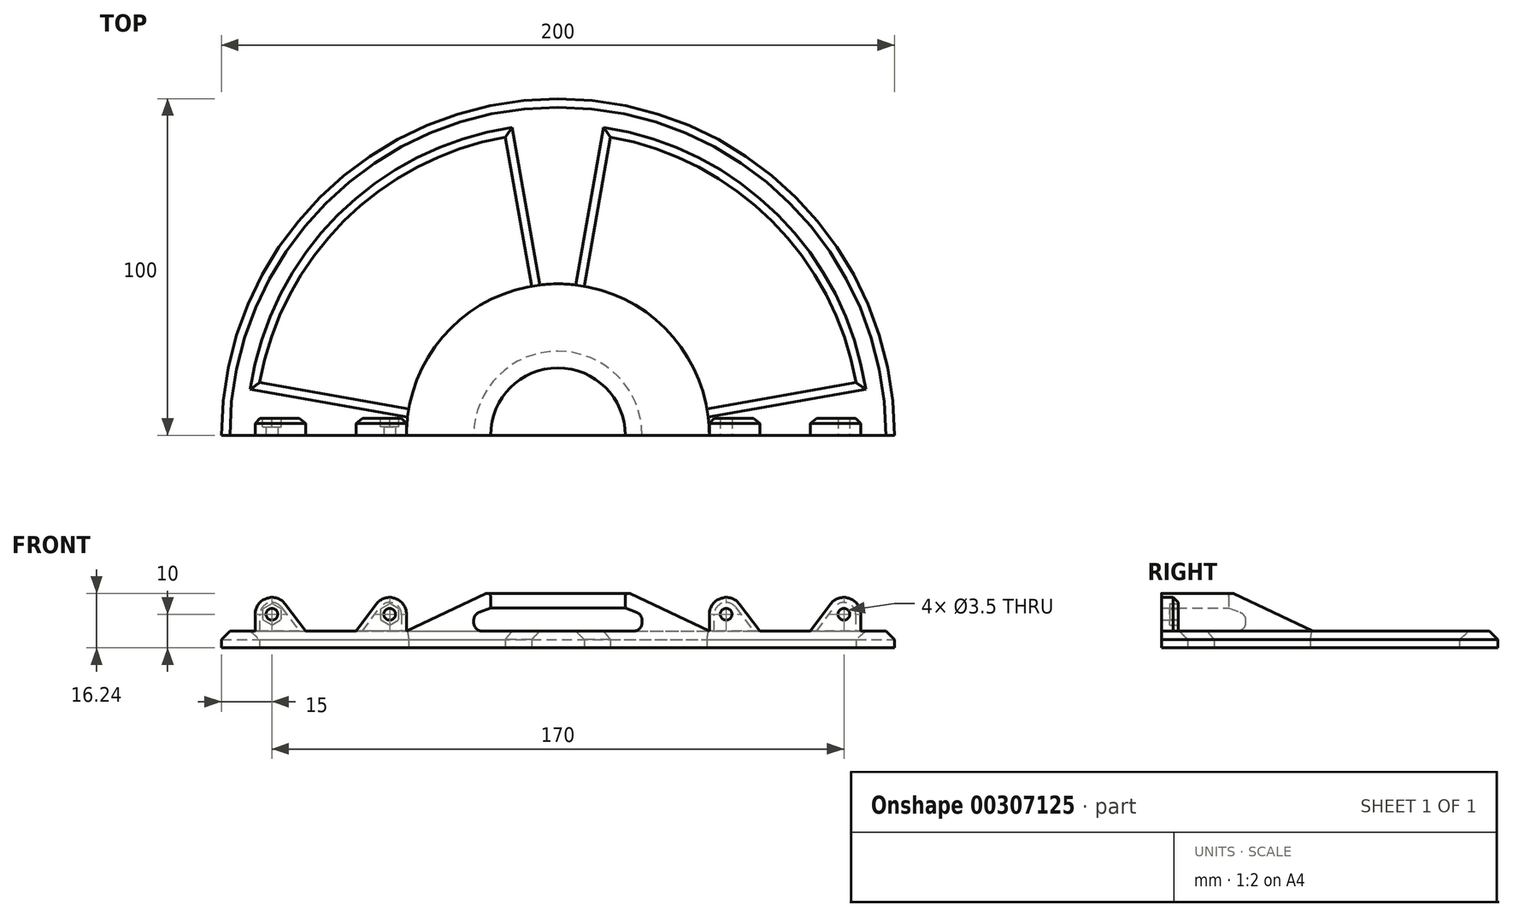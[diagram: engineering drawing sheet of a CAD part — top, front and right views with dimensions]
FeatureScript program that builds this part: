
annotation { "Feature Type Name" : "Feature", "Feature Type Description" : "" }
export const myFeature = defineFeature(function(context is Context, id is Id, definition is map)
    precondition{}
    {
        {
            var Q0;
            Q0=qCreatedBy(makeId("Front.planeOp"),FACE);
            var sketch = newSketch(context, id + "F0", { "sketchPlane" : qUnion([Q0])});
            skLineSegment(sketch, "E0", {"start": v(0, 0) * mm, "end": v(25, 0) * mm});
            skLineSegment(sketch, "E1", {"start": v(45, -5) * mm, "end": v(0, -5) * mm});
            skLineSegment(sketch, "E2", {"start": v(0, -5) * mm, "end": v(0, 0) * mm});
            skPoint(sketch, "E3.orphan", {"position": v(45, 0) * mm});
            skLineSegment(sketch, "E4", {"start": v(25, 0) * mm, "end": v(25, 5) * mm});
            skLineSegment(sketch, "E5", {"start": v(25, 5) * mm, "end": v(20, 6.82) * mm});
            skLineSegment(sketch, "E6", {"start": v(20, 6.82) * mm, "end": v(20, 11.82) * mm});
            skLineSegment(sketch, "E7", {"start": v(20, 11.82) * mm, "end": v(45, 0) * mm});
            skLineSegment(sketch, "E8", {"start": v(45, 0) * mm, "end": v(45, -5) * mm});
            skLineSegment(sketch, "E9.bottom", {"start": v(90, 0) * mm, "end": v(100, 0) * mm});
            skLineSegment(sketch, "E9.top", {"start": v(90, -5) * mm, "end": v(100, -5) * mm});
            skLineSegment(sketch, "E9.left", {"start": v(90, 0) * mm, "end": v(90, -5) * mm});
            skLineSegment(sketch, "E9.right", {"start": v(100, 0) * mm, "end": v(100, -5) * mm});
            skSolve(sketch);
        }
        {
            var Q0;
            Q0=qSketchRegion(id+"F0",true);
            var Q1;
            Q1=sQuery(id+"F0.wireOp",EDGE,"E2");
            revolve(context, id + "F1", {"entities" : qUnion([Q0]), "axis" : qUnion([Q1]), "revolveType" : RevolveType.ONE_DIRECTION, "angle" : 180 * degree});
        }
        {
            var Q0;
            Q0=makeQuery(id+"F1.opRevolve","SWEPT_EDGE",EDGE,{"disambiguationData":[OSD([sQuery(id+"F0.wireOp",EDGE,"E6"),sQuery(id+"F0.wireOp",EDGE,"E7")])]});
            var Q1;
            Q1=makeQuery(id+"Fz6hAyO1oWgQb9Q_1.boolean.opBoolean","INTERSECT",EDGE,{"derivedFrom":[makeQuery(id+"F1.opRevolve","SWEPT_FACE",FACE,{"disambiguationData":[OSD([sQuery(id+"F0.wireOp",EDGE,"E7")])]}),makeQuery(id+"Fz6hAyO1oWgQb9Q_1.opExtrude","SWEPT_FACE",FACE,{"disambiguationData":[OSD([sQuery(id+"FHeFj0AbrBGPQ3Y_1.wireOp",EDGE,"f4a93f66-89c4-4a73-b3e2-17d7893bedb9")])]})]});
            var Q2;
            Q2=makeQuery(id+"Fz6hAyO1oWgQb9Q_1.boolean.opBoolean","INTERSECT",EDGE,{"derivedFrom":[makeQuery(id+"F1.opRevolve","SWEPT_FACE",FACE,{"disambiguationData":[OSD([sQuery(id+"F0.wireOp",EDGE,"E7")])]}),makeQuery(id+"Fz6hAyO1oWgQb9Q_1.opExtrude","SWEPT_FACE",FACE,{"disambiguationData":[OSD([sQuery(id+"FHeFj0AbrBGPQ3Y_1.wireOp",EDGE,"73e09200-8e57-4483-a71f-662178566176")])]})]});
            var Q3;
            Q3=makeQuery(id+"Fz6hAyO1oWgQb9Q_1.boolean.opBoolean","INTERSECT",EDGE,{"derivedFrom":[makeQuery(id+"F1.opRevolve","SWEPT_FACE",FACE,{"disambiguationData":[OSD([sQuery(id+"F0.wireOp",EDGE,"E7")])]}),makeQuery(id+"Fz6hAyO1oWgQb9Q_1.opExtrude","SWEPT_FACE",FACE,{"disambiguationData":[OSD([sQuery(id+"FHeFj0AbrBGPQ3Y_1.wireOp",EDGE,"64aff4ee-1882-473b-a42a-8827de5f9001")])]})]});
            var Q4;
            Q4=makeQuery(id+"Fz6hAyO1oWgQb9Q_1.boolean.opBoolean","INTERSECT",EDGE,{"derivedFrom":[makeQuery(id+"F1.opRevolve","SWEPT_FACE",FACE,{"disambiguationData":[OSD([sQuery(id+"F0.wireOp",EDGE,"E7")])]}),makeQuery(id+"Fz6hAyO1oWgQb9Q_1.opExtrude","SWEPT_FACE",FACE,{"disambiguationData":[OSD([sQuery(id+"FHeFj0AbrBGPQ3Y_1.wireOp",EDGE,"ef642765-d67f-4a50-820b-96f5473efe75")])]})]});
            fillet(context, id + "F2", {"entities" : qUnion([Q0, Q1, Q2, Q3, Q4]), "radius" : 1 * mm, "tangentPropagation" : true, "allowEdgeOverflow" : false});
        }
        {
            var Q0;
            Q0=makeQuery(id+"F1.opRevolve","SWEPT_EDGE",EDGE,{"disambiguationData":[OSD([sQuery(id+"F0.wireOp",EDGE,"E4"),sQuery(id+"F0.wireOp",EDGE,"E5")])]});
            var Q1;
            Q1=makeQuery(id+"F1.opRevolve","SWEPT_EDGE",EDGE,{"disambiguationData":[OSD([sQuery(id+"F0.wireOp",EDGE,"E0"),sQuery(id+"F0.wireOp",EDGE,"E4")])]});
            fillet(context, id + "F3", {"entities" : qUnion([Q0, Q1]), "radius" : 2.5 * mm, "tangentPropagation" : true, "allowEdgeOverflow" : false});
        }
        {
            var Q0;
            Q0=makeQuery(id+"F1.opRevolve","CAP_FACE",FACE,{"disambiguationData":[OSD([sQuery(id+"F0.wireOp",EDGE,"E0"),sQuery(id+"F0.wireOp",EDGE,"E1"),sQuery(id+"F0.wireOp",EDGE,"E2"),sQuery(id+"F0.wireOp",EDGE,"E4"),sQuery(id+"F0.wireOp",EDGE,"E5"),sQuery(id+"F0.wireOp",EDGE,"E6"),sQuery(id+"F0.wireOp",EDGE,"E7"),sQuery(id+"F0.wireOp",EDGE,"E8")])],"isStart":true});
            var sketch = newSketch(context, id + "F4", { "sketchPlane" : qUnion([Q0])});
            skLineSegment(sketch, "E10.0", {"start": v(45, 0) * mm, "end": v(45, -5) * mm});
            skLineSegment(sketch, "E11.0", {"start": v(90, 0) * mm, "end": v(90, -5) * mm});
            skLineSegment(sketch, "E12", {"start": v(45, 0) * mm, "end": v(90, 0) * mm});
            skLineSegment(sketch, "E13", {"start": v(90, -5) * mm, "end": v(45, -5) * mm});
            skLineSegment(sketch, "E14", {"start": v(0, 0) * mm, "end": v(0, 20) * mm, "construction": true});
            skSolve(sketch);
        }
        {
            var Q0;
            Q0 = qSketchRegion(id + "F4", true);
            var Q1;
            Q1=sQuery(id+"F4.wireOp",EDGE,"E14");
            revolve(context, id + "F5", {"operationType" : NewBodyOperationType.ADD, "entities" : qUnion([Q0]), "axis" : qUnion([Q1]), "revolveType" : RevolveType.ONE_DIRECTION, "angle" : 10 * degree});
        }
        {
            var Q0;
            Q0=makeQuery(id+"F5.boolean.opBoolean","MERGE",FACE,{"derivedFrom":[makeQuery(id+"F1.opRevolve","CAP_FACE",FACE,{"disambiguationData":[OSD([sQuery(id+"F0.wireOp",EDGE,"E9.bottom"),sQuery(id+"F0.wireOp",EDGE,"E9.top"),sQuery(id+"F0.wireOp",EDGE,"E9.left"),sQuery(id+"F0.wireOp",EDGE,"E9.right")])],"isStart":true}),makeQuery(id+"F1.opRevolve","CAP_FACE",FACE,{"disambiguationData":[OSD([sQuery(id+"F0.wireOp",EDGE,"E0"),sQuery(id+"F0.wireOp",EDGE,"E1"),sQuery(id+"F0.wireOp",EDGE,"E2"),sQuery(id+"F0.wireOp",EDGE,"E4"),sQuery(id+"F0.wireOp",EDGE,"E5"),sQuery(id+"F0.wireOp",EDGE,"E6"),sQuery(id+"F0.wireOp",EDGE,"E7"),sQuery(id+"F0.wireOp",EDGE,"E8")])],"isStart":true}),makeQuery(id+"F5.opRevolve","CAP_FACE",FACE,{"disambiguationData":[OSD([sQuery(id+"F4.wireOp",EDGE,"E10.0"),sQuery(id+"F4.wireOp",EDGE,"E11.0"),sQuery(id+"F4.wireOp",EDGE,"E12"),sQuery(id+"F4.wireOp",EDGE,"E13")])],"isStart":true})]});
            var sketch = newSketch(context, id + "F6", { "sketchPlane" : qUnion([Q0])});
            skLineSegment(sketch, "E15.0", {"start": v(-90, 0) * mm, "end": v(-90, -5) * mm});
            skLineSegment(sketch, "E16.0", {"start": v(-45, 0) * mm, "end": v(-45, -5) * mm});
            skLineSegment(sketch, "E17", {"start": v(-90, 0) * mm, "end": v(-45, 0) * mm});
            skLineSegment(sketch, "E18", {"start": v(-45, -5) * mm, "end": v(-90, -5) * mm});
            skLineSegment(sketch, "E19", {"start": v(0, 0) * mm, "end": v(0, 20) * mm, "construction": true});
            skSolve(sketch);
        }
        {
            var Q0;
            Q0 = qSketchRegion(id + "F6", true);
            var Q1;
            Q1=sQuery(id+"F6.wireOp",EDGE,"E19");
            revolve(context, id + "F7", {"operationType" : NewBodyOperationType.ADD, "entities" : qUnion([Q0]), "axis" : qUnion([Q1]), "revolveType" : RevolveType.ONE_DIRECTION, "oppositeDirection" : true, "angle" : 10 * degree});
        }
        {
            var Q0;
            Q0=qCreatedBy(makeId("Right.planeOp"),FACE);
            var sketch = newSketch(context, id + "F8", { "sketchPlane" : qUnion([Q0])});
            skLineSegment(sketch, "E20", {"start": v(90, 0) * mm, "end": v(90, -5) * mm});
            skLineSegment(sketch, "E21", {"start": v(45, 0) * mm, "end": v(45, -5) * mm});
            skLineSegment(sketch, "E22", {"start": v(45, -5) * mm, "end": v(90, -5) * mm});
            skLineSegment(sketch, "E23", {"start": v(90, 0) * mm, "end": v(45, 0) * mm});
            skPoint(sketch, "E24.0", {"position": v(0, 0) * mm});
            skLineSegment(sketch, "E25", {"start": v(0, 0) * mm, "end": v(0, 20) * mm, "construction": true});
            skSolve(sketch);
        }
        {
            var Q0;
            Q0 = qSketchRegion(id + "F8", true);
            var Q1;
            Q1=sQuery(id+"F8.wireOp",EDGE,"E25");
            revolve(context, id + "F9", {"operationType" : NewBodyOperationType.ADD, "entities" : qUnion([Q0]), "axis" : qUnion([Q1]), "revolveType" : RevolveType.SYMMETRIC, "angle" : 20 * degree});
        }
        {
            var Q0;
            {var subQ0=sQuery(id+"F0.wireOp",EDGE,"E9.right");var subQ1=sQuery(id+"F0.wireOp",EDGE,"E9.left");var subQ2=sQuery(id+"F0.wireOp",EDGE,"E9.top");var subQ3=sQuery(id+"F0.wireOp",EDGE,"E9.bottom");Q0=makeQuery(id+"F7.boolean.opBoolean","MERGE",FACE,{"derivedFrom":[makeQuery(id+"F1.opRevolve","CAP_FACE",FACE,{"disambiguationData":[OSD([subQ3,subQ2,subQ1,subQ0])],"isStart":false}),makeQuery(id+"F5.boolean.opBoolean","MERGE",FACE,{"derivedFrom":[makeQuery(id+"F1.opRevolve","CAP_FACE",FACE,{"disambiguationData":[OSD([subQ3,subQ2,subQ1,subQ0])],"isStart":true}),makeQuery(id+"F1.opRevolve","CAP_FACE",FACE,{"disambiguationData":[OSD([sQuery(id+"F0.wireOp",EDGE,"E0"),sQuery(id+"F0.wireOp",EDGE,"E1"),sQuery(id+"F0.wireOp",EDGE,"E2"),sQuery(id+"F0.wireOp",EDGE,"E4"),sQuery(id+"F0.wireOp",EDGE,"E5"),sQuery(id+"F0.wireOp",EDGE,"E6"),sQuery(id+"F0.wireOp",EDGE,"E7"),sQuery(id+"F0.wireOp",EDGE,"E8")])],"isStart":true}),makeQuery(id+"F5.opRevolve","CAP_FACE",FACE,{"disambiguationData":[OSD([sQuery(id+"F4.wireOp",EDGE,"E10.0"),sQuery(id+"F4.wireOp",EDGE,"E11.0"),sQuery(id+"F4.wireOp",EDGE,"E12"),sQuery(id+"F4.wireOp",EDGE,"E13")])],"isStart":true})]}),makeQuery(id+"F7.opRevolve","CAP_FACE",FACE,{"disambiguationData":[OSD([sQuery(id+"F6.wireOp",EDGE,"E15.0"),sQuery(id+"F6.wireOp",EDGE,"E16.0"),sQuery(id+"F6.wireOp",EDGE,"E17"),sQuery(id+"F6.wireOp",EDGE,"E18")])],"isStart":true})]});}
            var sketch = newSketch(context, id + "F10", { "sketchPlane" : qUnion([Q0])});
            skLineSegment(sketch, "E26.0.0", {"start": v(45, 0) * mm, "end": v(21.43, 11.14) * mm, "construction": true});
            skArc(sketch, "E26.0.1", {"start": v(21.43, 11.14) * mm, "mid": v(20.46, 11.09) * mm, "end": v(20, 10.24) * mm, "construction": true});
            skLineSegment(sketch, "E26.0.2", {"start": v(20, 10.24) * mm, "end": v(20, 6.82) * mm, "construction": true});
            skLineSegment(sketch, "E26.0.3", {"start": v(20, 6.82) * mm, "end": v(23.36, 5.6) * mm, "construction": true});
            skArc(sketch, "E26.0.4", {"start": v(23.36, 5.6) * mm, "mid": v(24.55, 4.68) * mm, "end": v(25, 3.25) * mm, "construction": true});
            skLineSegment(sketch, "E26.0.5", {"start": v(25, 3.25) * mm, "end": v(25, 2.5) * mm, "construction": true});
            skArc(sketch, "E26.0.6", {"start": v(25, 2.5) * mm, "mid": v(24.27, 0.73) * mm, "end": v(22.5, 0) * mm, "construction": true});
            skLineSegment(sketch, "E26.0.7", {"start": v(22.5, 0) * mm, "end": v(-22.5, 0) * mm, "construction": true});
            skArc(sketch, "E26.0.8", {"start": v(-22.5, 0) * mm, "mid": v(-24.27, 0.73) * mm, "end": v(-25, 2.5) * mm, "construction": true});
            skLineSegment(sketch, "E26.0.9", {"start": v(-25, 2.5) * mm, "end": v(-25, 3.25) * mm, "construction": true});
            skArc(sketch, "E26.0.10", {"start": v(-25, 3.25) * mm, "mid": v(-24.55, 4.68) * mm, "end": v(-23.36, 5.6) * mm, "construction": true});
            skLineSegment(sketch, "E26.0.11", {"start": v(-23.36, 5.6) * mm, "end": v(-20, 6.82) * mm, "construction": true});
            skLineSegment(sketch, "E26.0.12", {"start": v(-20, 6.82) * mm, "end": v(-20, 10.24) * mm, "construction": true});
            skArc(sketch, "E26.0.13", {"start": v(-20, 10.24) * mm, "mid": v(-20.46, 11.09) * mm, "end": v(-21.43, 11.14) * mm, "construction": true});
            skLineSegment(sketch, "E26.0.14", {"start": v(-21.43, 11.14) * mm, "end": v(-45, 0) * mm, "construction": true});
            skLineSegment(sketch, "E26.0.15", {"start": v(-45, 0) * mm, "end": v(-100, 0) * mm, "construction": true});
            skLineSegment(sketch, "E26.0.16", {"start": v(-100, 0) * mm, "end": v(-100, -5) * mm, "construction": true});
            skLineSegment(sketch, "E26.0.17", {"start": v(-100, -5) * mm, "end": v(100, -5) * mm, "construction": true});
            skLineSegment(sketch, "E26.0.18", {"start": v(100, -5) * mm, "end": v(100, 0) * mm, "construction": true});
            skLineSegment(sketch, "E26.0.19", {"start": v(100, 0) * mm, "end": v(45, 0) * mm, "construction": true});
            skLineSegment(sketch, "E27", {"start": v(0, 0) * mm, "end": v(0, 30) * mm, "construction": true});
            skLineSegment(sketch, "E28.bottom", {"start": v(-90, 0) * mm, "end": v(-80, 0) * mm});
            skLineSegment(sketch, "E28.left", {"start": v(-90, 0) * mm, "end": v(-90, 5) * mm});
            skLineSegment(sketch, "E28.right", {"start": v(-80, 0) * mm, "end": v(-80, 5) * mm});
            skLineSegment(sketch, "E29.bottom", {"start": v(-45, 0) * mm, "end": v(-55, 0) * mm});
            skLineSegment(sketch, "E29.left", {"start": v(-45, 0) * mm, "end": v(-45, 5) * mm});
            skLineSegment(sketch, "E29.right", {"start": v(-55, 0) * mm, "end": v(-55, 5) * mm});
            skArc(sketch, "E30", {"start": v(-80, 5) * mm, "mid": v(-85, 10) * mm, "end": v(-90, 5) * mm});
            skArc(sketch, "E31", {"start": v(-45, 5) * mm, "mid": v(-50, 10) * mm, "end": v(-55, 5) * mm});
            skCircle(sketch, "E32", {"center": v(-50, 5) * mm, "radius": 1.75 * mm});
            skCircle(sketch, "E33", {"center": v(-85, 5) * mm, "radius": 1.75 * mm});
            skLineSegment(sketch, "E34.MirrorCS", {"start": v(80, 0) * mm, "end": v(80, 5) * mm});
            skLineSegment(sketch, "E35.MirrorCS", {"start": v(90, 0) * mm, "end": v(90, 5) * mm});
            skLineSegment(sketch, "E36.MirrorCS", {"start": v(55, 0) * mm, "end": v(55, 5) * mm});
            skLineSegment(sketch, "E37.MirrorCS", {"start": v(45, 0) * mm, "end": v(45, 5) * mm});
            skCircle(sketch, "E38.MirrorC", {"center": v(50, 5) * mm, "radius": 1.75 * mm});
            skCircle(sketch, "E39.MirrorC", {"center": v(85, 5) * mm, "radius": 1.75 * mm});
            skArc(sketch, "E40.MirrorCS", {"start": v(80, 5) * mm, "mid": v(85, 10) * mm, "end": v(90, 5) * mm});
            skLineSegment(sketch, "E41.MirrorCS", {"start": v(90, 0) * mm, "end": v(80, 0) * mm});
            skLineSegment(sketch, "E42.MirrorCS", {"start": v(100, 0) * mm, "end": v(100, -5) * mm, "construction": true});
            skLineSegment(sketch, "E43.MirrorCS", {"start": v(45, 0) * mm, "end": v(55, 0) * mm});
            skArc(sketch, "E44.MirrorCS", {"start": v(45, 5) * mm, "mid": v(50, 10) * mm, "end": v(55, 5) * mm});
            skSolve(sketch);
        }
        {
            var Q0;
            Q0 = qSketchRegion(id + "F10", true);
            extrude(context, id + "F11", {"entities" : qUnion([Q0]), "operationType" : NewBodyOperationType.ADD, "oppositeDirection" : true, "depth" : 5 * mm});
        }
        {
            var Q0;
            Q0=makeQuery(id+"F11.opExtrude","CAP_FACE",FACE,{"disambiguationData":[OSD([sQuery(id+"F10.wireOp",EDGE,"E29.bottom"),sQuery(id+"F10.wireOp",EDGE,"E29.left"),sQuery(id+"F10.wireOp",EDGE,"E29.right"),sQuery(id+"F10.wireOp",EDGE,"E31"),sQuery(id+"F10.wireOp",EDGE,"E32")])],"isStart":false});
            var sketch = newSketch(context, id + "F12", { "sketchPlane" : qUnion([Q0])});
            skCircle(sketch, "E45.cCircle", {"center": v(50, 5) * mm, "radius": 2.75 * mm, "construction": true});
            skLineSegment(sketch, "E45.0", {"start": v(52.75, 6.59) * mm, "end": v(52.75, 3.41) * mm});
            skLineSegment(sketch, "E45.1", {"start": v(52.75, 3.41) * mm, "end": v(50, 1.82) * mm});
            skLineSegment(sketch, "E45.2", {"start": v(50, 1.82) * mm, "end": v(47.25, 3.41) * mm});
            skLineSegment(sketch, "E45.3", {"start": v(47.25, 3.41) * mm, "end": v(47.25, 6.59) * mm});
            skLineSegment(sketch, "E45.4", {"start": v(47.25, 6.59) * mm, "end": v(50, 8.18) * mm});
            skLineSegment(sketch, "E45.5", {"start": v(50, 8.18) * mm, "end": v(52.75, 6.59) * mm});
            skPoint(sketch, "E45.0.midPoint", {"position": v(52.75, 5) * mm});
            skCircle(sketch, "E46.0", {"center": v(85, 5) * mm, "radius": 1.75 * mm, "construction": true});
            skCircle(sketch, "E47.cCircle", {"center": v(85, 5) * mm, "radius": 2.75 * mm, "construction": true});
            skLineSegment(sketch, "E47.0", {"start": v(82.25, 3.41) * mm, "end": v(82.25, 6.59) * mm});
            skLineSegment(sketch, "E47.1", {"start": v(82.25, 6.59) * mm, "end": v(85, 8.18) * mm});
            skLineSegment(sketch, "E47.2", {"start": v(85, 8.18) * mm, "end": v(87.75, 6.59) * mm});
            skLineSegment(sketch, "E47.3", {"start": v(87.75, 6.59) * mm, "end": v(87.75, 3.41) * mm});
            skLineSegment(sketch, "E47.4", {"start": v(87.75, 3.41) * mm, "end": v(85, 1.82) * mm});
            skLineSegment(sketch, "E47.5", {"start": v(85, 1.82) * mm, "end": v(82.25, 3.41) * mm});
            skPoint(sketch, "E47.0.midPoint", {"position": v(82.25, 5) * mm});
            skSolve(sketch);
        }
        {
            var Q0;
            Q0 = qSketchRegion(id + "F12", true);
            extrude(context, id + "F13", {"entities" : qUnion([Q0]), "operationType" : NewBodyOperationType.REMOVE, "oppositeDirection" : true, "depth" : 2.5 * mm});
        }
        {
            var Q0;
            Q0=makeQuery(id+"F9.opRevolve","CAP_EDGE",EDGE,{"disambiguationData":[OSD([sQuery(id+"F8.wireOp",EDGE,"E23")])],"isStart":false});
            var Q1;
            Q1=makeQuery(id+"F9.opRevolve","CAP_EDGE",EDGE,{"disambiguationData":[OSD([sQuery(id+"F8.wireOp",EDGE,"E23")])],"isStart":true});
            var Q2;
            {var subQ0=sQuery(id+"F6.wireOp",EDGE,"E17");var subQ1=sQuery(id+"F0.wireOp",EDGE,"E9.left");var subQ2=sQuery(id+"F0.wireOp",EDGE,"E9.bottom");Q2=makeQuery(id+"F9.boolean.opBoolean","SPLIT",EDGE,{"disambiguationData":[TD([makeQuery(id+"F7.opRevolve","CAP_FACE",FACE,{"disambiguationData":[OSD([sQuery(id+"F6.wireOp",EDGE,"E15.0"),sQuery(id+"F6.wireOp",EDGE,"E16.0"),subQ0,sQuery(id+"F6.wireOp",EDGE,"E18")])],"isStart":false})])],"derivedFrom":makeQuery(id+"F1.opRevolve","SWEPT_EDGE",EDGE,{"disambiguationData":[OSD([subQ2,subQ1])]})});}
            var Q3;
            Q3=makeQuery(id+"F7.opRevolve","CAP_EDGE",EDGE,{"disambiguationData":[OSD([sQuery(id+"F6.wireOp",EDGE,"E17")])],"isStart":false});
            var Q4;
            Q4=makeQuery(id+"F5.opRevolve","CAP_EDGE",EDGE,{"disambiguationData":[OSD([sQuery(id+"F4.wireOp",EDGE,"E12")])],"isStart":false});
            var Q5;
            {var subQ0=sQuery(id+"F4.wireOp",EDGE,"E12");var subQ2=sQuery(id+"F0.wireOp",EDGE,"E9.left");var subQ3=sQuery(id+"F0.wireOp",EDGE,"E9.bottom");Q5=makeQuery(id+"F9.boolean.opBoolean","SPLIT",EDGE,{"disambiguationData":[TD([makeQuery(id+"F5.opRevolve","CAP_FACE",FACE,{"disambiguationData":[OSD([sQuery(id+"F4.wireOp",EDGE,"E10.0"),sQuery(id+"F4.wireOp",EDGE,"E11.0"),subQ0,sQuery(id+"F4.wireOp",EDGE,"E13")])],"isStart":false})])],"derivedFrom":makeQuery(id+"F1.opRevolve","SWEPT_EDGE",EDGE,{"disambiguationData":[OSD([subQ3,subQ2])]})});}
            var Q6;
            Q6=makeQuery(id+"F1.opRevolve","SWEPT_EDGE",EDGE,{"disambiguationData":[OSD([sQuery(id+"F0.wireOp",EDGE,"E9.bottom"),sQuery(id+"F0.wireOp",EDGE,"E9.right")])]});
            chamfer(context, id + "F14", {"entities" : qUnion([Q0, Q1, Q2, Q3, Q4, Q5, Q6]), "width" : 2.5 * mm, "tangentPropagation" : true});
        }
        {
            var Q0;
            {var subQ0=sQuery(id+"F0.wireOp",EDGE,"E9.right");var subQ1=sQuery(id+"F0.wireOp",EDGE,"E9.left");var subQ2=sQuery(id+"F0.wireOp",EDGE,"E9.top");var subQ3=sQuery(id+"F0.wireOp",EDGE,"E9.bottom");Q0=makeQuery(id+"F11.boolean.opBoolean","MERGE",FACE,{"derivedFrom":[makeQuery(id+"F7.boolean.opBoolean","MERGE",FACE,{"derivedFrom":[makeQuery(id+"F1.opRevolve","CAP_FACE",FACE,{"disambiguationData":[OSD([subQ3,subQ2,subQ1,subQ0])],"isStart":false}),makeQuery(id+"F5.boolean.opBoolean","MERGE",FACE,{"derivedFrom":[makeQuery(id+"F1.opRevolve","CAP_FACE",FACE,{"disambiguationData":[OSD([subQ3,subQ2,subQ1,subQ0])],"isStart":true}),makeQuery(id+"F1.opRevolve","CAP_FACE",FACE,{"disambiguationData":[OSD([sQuery(id+"F0.wireOp",EDGE,"E0"),sQuery(id+"F0.wireOp",EDGE,"E1"),sQuery(id+"F0.wireOp",EDGE,"E2"),sQuery(id+"F0.wireOp",EDGE,"E4"),sQuery(id+"F0.wireOp",EDGE,"E5"),sQuery(id+"F0.wireOp",EDGE,"E6"),sQuery(id+"F0.wireOp",EDGE,"E7"),sQuery(id+"F0.wireOp",EDGE,"E8")])],"isStart":true}),makeQuery(id+"F5.opRevolve","CAP_FACE",FACE,{"disambiguationData":[OSD([sQuery(id+"F4.wireOp",EDGE,"E10.0"),sQuery(id+"F4.wireOp",EDGE,"E11.0"),sQuery(id+"F4.wireOp",EDGE,"E12"),sQuery(id+"F4.wireOp",EDGE,"E13")])],"isStart":true})]}),makeQuery(id+"F7.opRevolve","CAP_FACE",FACE,{"disambiguationData":[OSD([sQuery(id+"F6.wireOp",EDGE,"E15.0"),sQuery(id+"F6.wireOp",EDGE,"E16.0"),sQuery(id+"F6.wireOp",EDGE,"E17"),sQuery(id+"F6.wireOp",EDGE,"E18")])],"isStart":true})]}),makeQuery(id+"F11.opExtrude","CAP_FACE",FACE,{"disambiguationData":[OSD([sQuery(id+"F10.wireOp",EDGE,"E28.bottom"),sQuery(id+"F10.wireOp",EDGE,"E28.left"),sQuery(id+"F10.wireOp",EDGE,"E28.right"),sQuery(id+"F10.wireOp",EDGE,"E30"),sQuery(id+"F10.wireOp",EDGE,"E33")])],"isStart":true}),makeQuery(id+"F11.opExtrude","CAP_FACE",FACE,{"disambiguationData":[OSD([sQuery(id+"F10.wireOp",EDGE,"E29.bottom"),sQuery(id+"F10.wireOp",EDGE,"E29.left"),sQuery(id+"F10.wireOp",EDGE,"E29.right"),sQuery(id+"F10.wireOp",EDGE,"E31"),sQuery(id+"F10.wireOp",EDGE,"E32")])],"isStart":true}),makeQuery(id+"F11.opExtrude","CAP_FACE",FACE,{"disambiguationData":[OSD([sQuery(id+"F10.wireOp",EDGE,"E34.MirrorCS"),sQuery(id+"F10.wireOp",EDGE,"E35.MirrorCS"),sQuery(id+"F10.wireOp",EDGE,"E39.MirrorC"),sQuery(id+"F10.wireOp",EDGE,"E40.MirrorCS"),sQuery(id+"F10.wireOp",EDGE,"E41.MirrorCS")])],"isStart":true}),makeQuery(id+"F11.opExtrude","CAP_FACE",FACE,{"disambiguationData":[OSD([sQuery(id+"F10.wireOp",EDGE,"E36.MirrorCS"),sQuery(id+"F10.wireOp",EDGE,"E37.MirrorCS"),sQuery(id+"F10.wireOp",EDGE,"E38.MirrorC"),sQuery(id+"F10.wireOp",EDGE,"E43.MirrorCS"),sQuery(id+"F10.wireOp",EDGE,"E44.MirrorCS")])],"isStart":true})]});}
            var sketch = newSketch(context, id + "F15", { "sketchPlane" : qUnion([Q0])});
            skLineSegment(sketch, "E48", {"start": v(-75, 0) * mm, "end": v(-81, 8) * mm});
            skArc(sketch, "E49.0", {"start": v(-80, 5) * mm, "mid": v(-80.26, 6.58) * mm, "end": v(-81, 8) * mm});
            skPoint(sketch, "E50.0", {"position": v(-80, 2.5) * mm});
            skLineSegment(sketch, "E51.0", {"start": v(-80, 0) * mm, "end": v(-80, 5) * mm});
            skLineSegment(sketch, "E52", {"start": v(-80, 0) * mm, "end": v(-75, 0) * mm});
            skPoint(sketch, "E53.orphan", {"position": v(-90, 5) * mm});
            skLineSegment(sketch, "E54", {"start": v(-67.5, 0) * mm, "end": v(-67.5, 10) * mm, "construction": true});
            skLineSegment(sketch, "E55.MirrorCS", {"start": v(-55, 0) * mm, "end": v(-55, 5) * mm});
            skLineSegment(sketch, "E56.MirrorCS", {"start": v(-60, 0) * mm, "end": v(-54, 8) * mm});
            skLineSegment(sketch, "E57.MirrorCS", {"start": v(-55, 0) * mm, "end": v(-60, 0) * mm});
            skArc(sketch, "E58.MirrorCS", {"start": v(-55, 5) * mm, "mid": v(-54.74, 6.58) * mm, "end": v(-54, 8) * mm});
            skPoint(sketch, "E59.MirrorP", {"position": v(-55, 2.5) * mm});
            skLineSegment(sketch, "E60", {"start": v(0, 0) * mm, "end": v(0, 20) * mm, "construction": true});
            skArc(sketch, "E61.MirrorCS", {"start": v(55, 5) * mm, "mid": v(54.74, 6.58) * mm, "end": v(54, 8) * mm});
            skArc(sketch, "E62.MirrorCS", {"start": v(80, 5) * mm, "mid": v(80.26, 6.58) * mm, "end": v(81, 8) * mm});
            skLineSegment(sketch, "E63.MirrorCS", {"start": v(55, 0) * mm, "end": v(55, 5) * mm});
            skLineSegment(sketch, "E64.MirrorCS", {"start": v(80, 0) * mm, "end": v(80, 5) * mm});
            skPoint(sketch, "E65.MirrorP", {"position": v(80, 2.5) * mm});
            skPoint(sketch, "E66.MirrorP", {"position": v(55, 2.5) * mm});
            skLineSegment(sketch, "E67.MirrorCS", {"start": v(80, 0) * mm, "end": v(75, 0) * mm});
            skLineSegment(sketch, "E68.MirrorCS", {"start": v(60, 0) * mm, "end": v(54, 8) * mm});
            skLineSegment(sketch, "E69.MirrorCS", {"start": v(75, 0) * mm, "end": v(81, 8) * mm});
            skLineSegment(sketch, "E70.MirrorCS", {"start": v(67.5, 0) * mm, "end": v(67.5, 10) * mm, "construction": true});
            skLineSegment(sketch, "E71.MirrorCS", {"start": v(55, 0) * mm, "end": v(60, 0) * mm});
            skSolve(sketch);
        }
        {
            var Q0;
            Q0 = qSketchRegion(id + "F15", true);
            var Q1;
            Q1=makeQuery(id+"F11.opExtrude","CAP_FACE",FACE,{"disambiguationData":[OSD([sQuery(id+"F10.wireOp",EDGE,"E29.bottom"),sQuery(id+"F10.wireOp",EDGE,"E29.left"),sQuery(id+"F10.wireOp",EDGE,"E29.right"),sQuery(id+"F10.wireOp",EDGE,"E31"),sQuery(id+"F10.wireOp",EDGE,"E32")])],"isStart":false});
            extrude(context, id + "F16", {"entities" : qUnion([Q0]), "operationType" : NewBodyOperationType.ADD, "endBound" : BoundingType.UP_TO_SURFACE, "oppositeDirection" : true, "endBoundEntityFace" : qUnion([Q1]), "depth" : 25 * mm});
        }
        {
            var Q0;
            Q0=makeQuery(id+"F16.opExtrude","CAP_EDGE",EDGE,{"disambiguationData":[OSD([sQuery(id+"F15.wireOp",EDGE,"E56.MirrorCS")])],"isStart":false});
            var Q1;
            Q1=makeQuery(id+"F16.opExtrude","CAP_EDGE",EDGE,{"disambiguationData":[OSD([sQuery(id+"F15.wireOp",EDGE,"E48")])],"isStart":false});
            var Q2;
            Q2=makeQuery(id+"F16.opExtrude","CAP_EDGE",EDGE,{"disambiguationData":[OSD([sQuery(id+"F15.wireOp",EDGE,"E69.MirrorCS")])],"isStart":false});
            var Q3;
            Q3=makeQuery(id+"F16.opExtrude","CAP_EDGE",EDGE,{"disambiguationData":[OSD([sQuery(id+"F15.wireOp",EDGE,"E68.MirrorCS")])],"isStart":false});
            chamfer(context, id + "F17", {"entities" : qUnion([Q0, Q1, Q2, Q3]), "width" : 1.5 * mm, "tangentPropagation" : true});
        }
    });
